# Revit family: Shower-Valves_and_Controls-KOHLER-Rite_Temp-K-11748
name_source: partatom
category: Pipe Accessories
revit_build: Autodesk Revit 2015 (Build: 20140606_1530(x64)
units: mm (PartAtom-declared; Revit-internal decimal feet)

## types (2) — shared parameters
ADA Compliant = No
Assembly Code = D2020
Cold Water Inlet = Cold Water Inlet
Date Modified = 08/02/2018
Default Elevation = 36"
Finish = Kohler-Metal-Brass
Flow Rate = 5 GPM
Height = 5 13/16"
Hot Water Inlet = Hot Water Inlet
Length = 2 3/4"
Manufacturer = KOHLER Co.
MasterFormat 1995 = 154300
MasterFormat 2004 = 22.11.00
Material = Brass Construction
Pressure = 0.00 psi
Product Documentation Link = http://www.us.kohler.com
Product Name = Rite-Temp
Product Page URL = http://www.us.kohler.com
Tempered Water Outlet 1 = Tempered Water Outlet 1
Tempered Water Outlet 2 = Tempered Water Outlet 2
URL = https://www.us.kohler.com
Waste Water Outlet = Waste Water Outlet

## per-type parameters (varying)
| type | 11748_K | 11748_KS | Description | Model | Type | Width |
| Push-button diverter valve | Yes | No | 1/2inch pressure-balancing valve with push-button diverter | K-11748-K | 1 | 4" |
| Push-button diverter and screwdriver stops valve | No | Yes | 1/2inch pressure-balancing valve with push-button diverter and screwdriver stops | K-11748-KS | 2 | 5 3/4" |

## geometry (parser evidence)
native form markers: Sweep x7
no freeform markers — native parametric forms only
